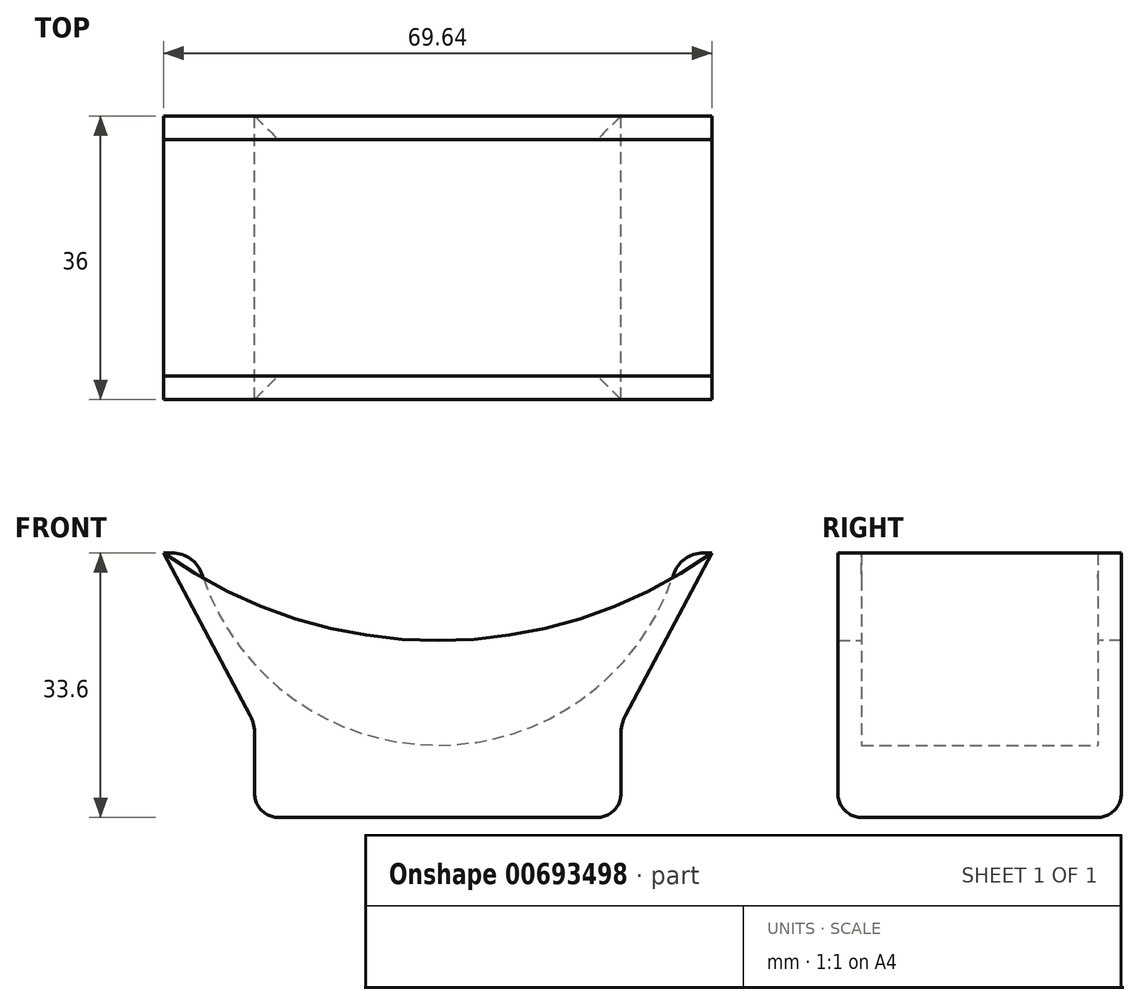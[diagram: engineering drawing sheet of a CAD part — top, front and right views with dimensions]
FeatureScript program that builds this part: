
annotation { "Feature Type Name" : "Feature", "Feature Type Description" : "" }
export const myFeature = defineFeature(function(context is Context, id is Id, definition is map)
    precondition{}
    {
        {
            var Q0;
            Q0=qCreatedBy(makeId("Front.planeOp"),FACE);
            var sketch = newSketch(context, id + "F0", { "sketchPlane" : qUnion([Q0])});
            skLineSegment(sketch, "E0", {"start": v(0, 0) * mm, "end": v(23.26, 0) * mm});
            skLineSegment(sketch, "E1", {"start": v(23.26, 0) * mm, "end": v(23.26, 11.86) * mm});
            skLineSegment(sketch, "E2", {"start": v(23.26, 11.86) * mm, "end": v(34.82, 33.6) * mm});
            skLineSegment(sketch, "E3", {"start": v(0, -60.61) * mm, "end": v(0, 88) * mm, "construction": true});
            skArc(sketch, "E4", {"start": v(-30.7, 33.6) * mm, "mid": v(0, 9.17) * mm, "end": v(30.7, 33.6) * mm});
            skLineSegment(sketch, "E5", {"start": v(30.7, 33.6) * mm, "end": v(34.82, 33.6) * mm});
            skLineSegment(sketch, "E6.MirrorCS", {"start": v(0, 0) * mm, "end": v(-23.26, 0) * mm});
            skLineSegment(sketch, "E7.MirrorCS", {"start": v(-23.26, 0) * mm, "end": v(-23.26, 11.86) * mm});
            skLineSegment(sketch, "E8.MirrorCS", {"start": v(-23.26, 11.86) * mm, "end": v(-34.82, 33.6) * mm});
            skLineSegment(sketch, "E9.MirrorCS", {"start": v(-30.7, 33.6) * mm, "end": v(-34.82, 33.6) * mm});
            skSolve(sketch);
        }
        {
            var Q0;
            Q0=makeQuery(id+"F0.imprint","IMPRINT",FACE,{"disambiguationData":[TD([[makeQuery(id+"F0.imprint","IMPRINT",EDGE,{"derivedFrom":sQuery(id+"F0.wireOp",EDGE,"E0")}),1.0]])]});
            extrude(context, id + "F1", {"entities" : qUnion([Q0]), "depth" : 30 * mm, "offsetDistance" : 25 * mm});
        }
        {
            var Q0;
            Q0=makeQuery(id+"F1.opExtrude","CAP_FACE",FACE,{"disambiguationData":[OSD([sQuery(id+"F0.wireOp",EDGE,"E0"),sQuery(id+"F0.wireOp",EDGE,"E1"),sQuery(id+"F0.wireOp",EDGE,"E2"),sQuery(id+"F0.wireOp",EDGE,"E4"),sQuery(id+"F0.wireOp",EDGE,"E5"),sQuery(id+"F0.wireOp",EDGE,"E6.MirrorCS"),sQuery(id+"F0.wireOp",EDGE,"E7.MirrorCS"),sQuery(id+"F0.wireOp",EDGE,"E8.MirrorCS"),sQuery(id+"F0.wireOp",EDGE,"E9.MirrorCS")])],"isStart":false});
            var sketch = newSketch(context, id + "F2", { "sketchPlane" : qUnion([Q0])});
            skArc(sketch, "E10", {"start": v(-34.82, 33.6) * mm, "mid": v(0, 22.46) * mm, "end": v(34.82, 33.6) * mm});
            skLineSegment(sketch, "E11", {"start": v(-34.82, 33.6) * mm, "end": v(-23.26, 11.86) * mm});
            skLineSegment(sketch, "E12", {"start": v(-23.26, 11.86) * mm, "end": v(-23.26, 0) * mm});
            skLineSegment(sketch, "E13", {"start": v(-23.26, 0) * mm, "end": v(23.26, 0) * mm});
            skLineSegment(sketch, "E14", {"start": v(23.26, 0) * mm, "end": v(23.26, 11.86) * mm});
            skLineSegment(sketch, "E15", {"start": v(23.26, 11.86) * mm, "end": v(34.82, 33.6) * mm});
            skSolve(sketch);
        }
        {
            var Q0;
            Q0 = qSketchRegion(id + "F2", true);
            extrude(context, id + "F3", {"entities" : qUnion([Q0]), "operationType" : NewBodyOperationType.ADD, "depth" : 3 * mm, "offsetDistance" : 25 * mm});
        }
        {
            var Q0;
            Q0=makeQuery(id+"F1.opExtrude","CAP_FACE",FACE,{"disambiguationData":[OSD([sQuery(id+"F0.wireOp",EDGE,"E0"),sQuery(id+"F0.wireOp",EDGE,"E1"),sQuery(id+"F0.wireOp",EDGE,"E2"),sQuery(id+"F0.wireOp",EDGE,"E4"),sQuery(id+"F0.wireOp",EDGE,"E5"),sQuery(id+"F0.wireOp",EDGE,"E6.MirrorCS"),sQuery(id+"F0.wireOp",EDGE,"E7.MirrorCS"),sQuery(id+"F0.wireOp",EDGE,"E8.MirrorCS"),sQuery(id+"F0.wireOp",EDGE,"E9.MirrorCS")])],"isStart":true});
            var sketch = newSketch(context, id + "F4", { "sketchPlane" : qUnion([Q0])});
            skArc(sketch, "E16", {"start": v(-34.82, 33.6) * mm, "mid": v(0, 22.46) * mm, "end": v(34.82, 33.6) * mm});
            skLineSegment(sketch, "E17", {"start": v(-34.82, 33.6) * mm, "end": v(-23.26, 11.86) * mm});
            skLineSegment(sketch, "E18", {"start": v(-23.26, 11.86) * mm, "end": v(-23.26, 0) * mm});
            skLineSegment(sketch, "E19", {"start": v(-23.26, 0) * mm, "end": v(23.26, 0) * mm});
            skLineSegment(sketch, "E20", {"start": v(23.26, 0) * mm, "end": v(23.26, 11.86) * mm});
            skLineSegment(sketch, "E21", {"start": v(23.26, 11.86) * mm, "end": v(34.82, 33.6) * mm});
            skSolve(sketch);
        }
        {
            var Q0;
            Q0 = qSketchRegion(id + "F4", true);
            extrude(context, id + "F5", {"entities" : qUnion([Q0]), "operationType" : NewBodyOperationType.ADD, "depth" : 3 * mm, "offsetDistance" : 25 * mm});
        }
        {
            var Q0;
            Q0=makeQuery(id+"F1.opExtrude","SWEPT_EDGE",EDGE,{"disambiguationData":[OSD([sQuery(id+"F0.wireOp",EDGE,"E4"),sQuery(id+"F0.wireOp",EDGE,"E5")])]});
            var Q1;
            Q1=makeQuery(id+"F1.opExtrude","SWEPT_EDGE",EDGE,{"disambiguationData":[OSD([sQuery(id+"F0.wireOp",EDGE,"E4"),sQuery(id+"F0.wireOp",EDGE,"E9.MirrorCS")])]});
            fillet(context, id + "F6", {"entities" : qUnion([Q0, Q1]), "radius" : 4 * mm, "tangentPropagation" : true, "allowEdgeOverflow" : false});
        }
        {
            var Q0;
            Q0=makeQuery(id+"F5.boolean.opBoolean","MERGE",EDGE,{"derivedFrom":[makeQuery(id+"F3.boolean.opBoolean","MERGE",EDGE,{"derivedFrom":[makeQuery(id+"F1.opExtrude","SWEPT_EDGE",EDGE,{"disambiguationData":[OSD([sQuery(id+"F0.wireOp",EDGE,"E0"),sQuery(id+"F0.wireOp",EDGE,"E1")])]}),makeQuery(id+"F3.opExtrude","SWEPT_EDGE",EDGE,{"disambiguationData":[OSD([sQuery(id+"F2.wireOp",EDGE,"E13"),sQuery(id+"F2.wireOp",EDGE,"E14")])]})]}),makeQuery(id+"F5.opExtrude","SWEPT_EDGE",EDGE,{"disambiguationData":[OSD([sQuery(id+"F4.wireOp",EDGE,"E18"),sQuery(id+"F4.wireOp",EDGE,"E19")])]})]});
            var Q1;
            Q1=makeQuery(id+"F5.opExtrude","CAP_EDGE",EDGE,{"disambiguationData":[OSD([sQuery(id+"F4.wireOp",EDGE,"E19")])],"isStart":false});
            var Q2;
            Q2=makeQuery(id+"F5.boolean.opBoolean","MERGE",EDGE,{"derivedFrom":[makeQuery(id+"F3.boolean.opBoolean","MERGE",EDGE,{"derivedFrom":[makeQuery(id+"F1.opExtrude","SWEPT_EDGE",EDGE,{"disambiguationData":[OSD([sQuery(id+"F0.wireOp",EDGE,"E6.MirrorCS"),sQuery(id+"F0.wireOp",EDGE,"E7.MirrorCS")])]}),makeQuery(id+"F3.opExtrude","SWEPT_EDGE",EDGE,{"disambiguationData":[OSD([sQuery(id+"F2.wireOp",EDGE,"E12"),sQuery(id+"F2.wireOp",EDGE,"E13")])]})]}),makeQuery(id+"F5.opExtrude","SWEPT_EDGE",EDGE,{"disambiguationData":[OSD([sQuery(id+"F4.wireOp",EDGE,"E19"),sQuery(id+"F4.wireOp",EDGE,"E20")])]})]});
            var Q3;
            Q3=makeQuery(id+"F3.opExtrude","CAP_EDGE",EDGE,{"disambiguationData":[OSD([sQuery(id+"F2.wireOp",EDGE,"E13")])],"isStart":false});
            fillet(context, id + "F7", {"entities" : qUnion([Q0, Q1, Q2, Q3]), "radius" : 3 * mm, "tangentPropagation" : true, "allowEdgeOverflow" : false});
        }
        {
            var Q0;
            Q0=makeQuery(id+"F5.boolean.opBoolean","MERGE",EDGE,{"derivedFrom":[makeQuery(id+"F3.boolean.opBoolean","MERGE",EDGE,{"derivedFrom":[makeQuery(id+"F1.opExtrude","SWEPT_EDGE",EDGE,{"disambiguationData":[OSD([sQuery(id+"F0.wireOp",EDGE,"E7.MirrorCS"),sQuery(id+"F0.wireOp",EDGE,"E8.MirrorCS")])]}),makeQuery(id+"F3.opExtrude","SWEPT_EDGE",EDGE,{"disambiguationData":[OSD([sQuery(id+"F2.wireOp",EDGE,"E11"),sQuery(id+"F2.wireOp",EDGE,"E12")])]})]}),makeQuery(id+"F5.opExtrude","SWEPT_EDGE",EDGE,{"disambiguationData":[OSD([sQuery(id+"F4.wireOp",EDGE,"E20"),sQuery(id+"F4.wireOp",EDGE,"E21")])]})]});
            var Q1;
            Q1=makeQuery(id+"F5.boolean.opBoolean","MERGE",EDGE,{"derivedFrom":[makeQuery(id+"F3.boolean.opBoolean","MERGE",EDGE,{"derivedFrom":[makeQuery(id+"F1.opExtrude","SWEPT_EDGE",EDGE,{"disambiguationData":[OSD([sQuery(id+"F0.wireOp",EDGE,"E1"),sQuery(id+"F0.wireOp",EDGE,"E2")])]}),makeQuery(id+"F3.opExtrude","SWEPT_EDGE",EDGE,{"disambiguationData":[OSD([sQuery(id+"F2.wireOp",EDGE,"E14"),sQuery(id+"F2.wireOp",EDGE,"E15")])]})]}),makeQuery(id+"F5.opExtrude","SWEPT_EDGE",EDGE,{"disambiguationData":[OSD([sQuery(id+"F4.wireOp",EDGE,"E17"),sQuery(id+"F4.wireOp",EDGE,"E18")])]})]});
            fillet(context, id + "F8", {"entities" : qUnion([Q0, Q1]), "radius" : 5.1 * mm, "tangentPropagation" : true, "allowEdgeOverflow" : false});
        }
    });
